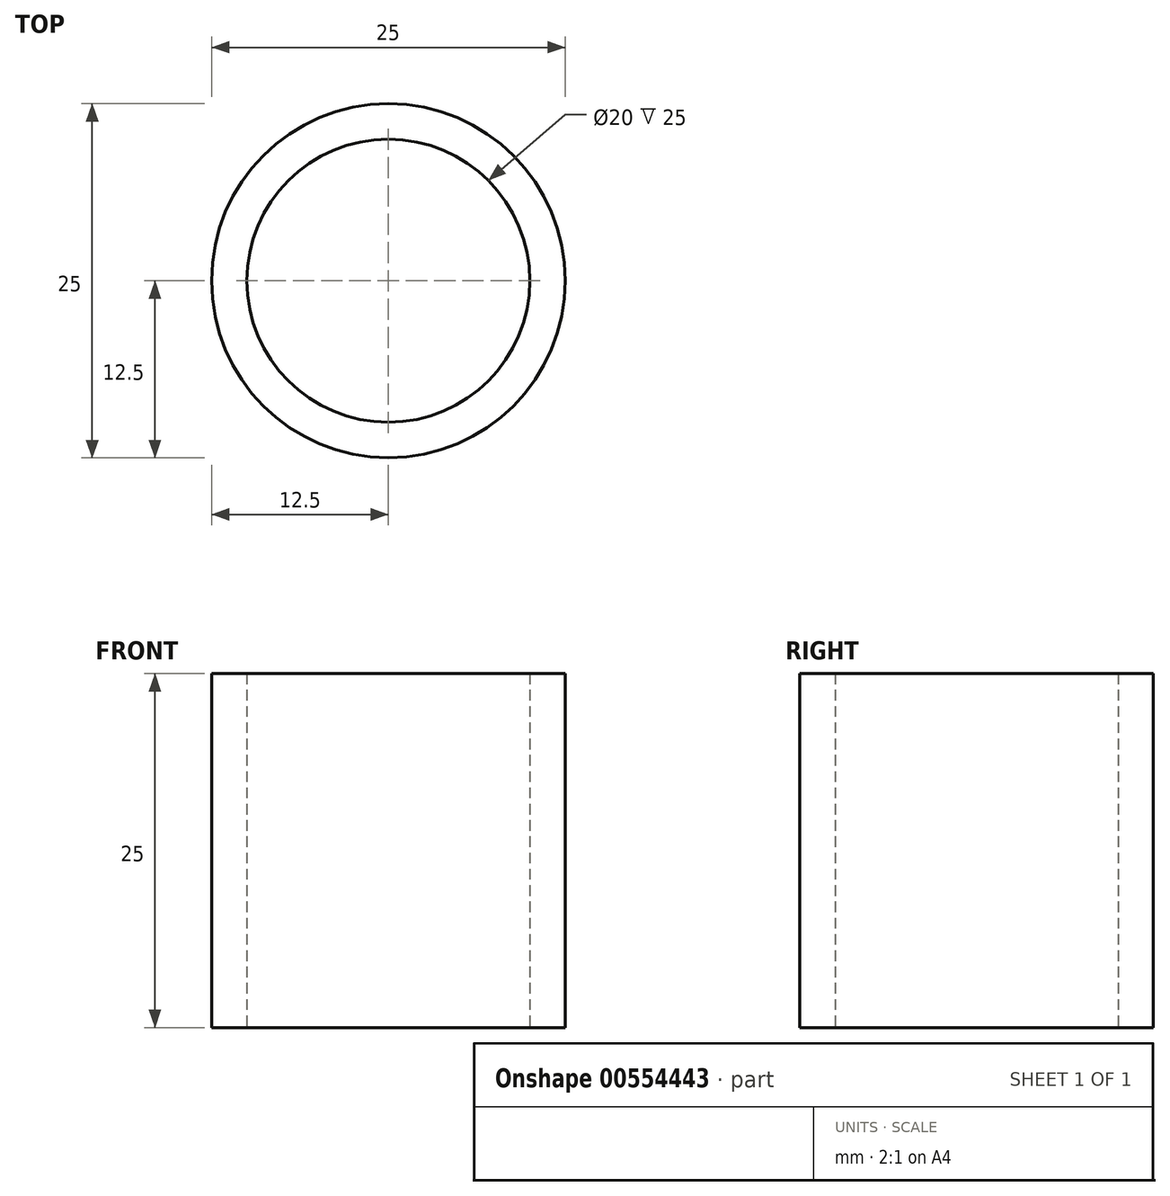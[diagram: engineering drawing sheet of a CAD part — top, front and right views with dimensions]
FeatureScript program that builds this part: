
annotation { "Feature Type Name" : "Feature", "Feature Type Description" : "" }
export const myFeature = defineFeature(function(context is Context, id is Id, definition is map)
    precondition{}
    {
        {
            var Q0;
            Q0=qCreatedBy(makeId("Top.planeOp"),FACE);
            var sketch = newSketch(context, id + "F0", { "sketchPlane" : qUnion([Q0])});
            skCircle(sketch, "E0", {"center": v(0, 0) * mm, "radius": 12.5 * mm});
            skCircle(sketch, "E1", {"center": v(0, 0) * mm, "radius": 10 * mm});
            skSolve(sketch);
        }
        {
            var Q0;
            Q0=makeQuery(id+"F0.imprint","IMPRINT",FACE,{"disambiguationData":[TD([[makeQuery(id+"F0.imprint","IMPRINT",EDGE,{"derivedFrom":sQuery(id+"F0.wireOp",EDGE,"E0")}),1.0]])]});
            extrude(context, id + "F1", {"entities" : qUnion([Q0]), "depth" : 25 * mm, "offsetDistance" : 25 * mm});
        }
    });
